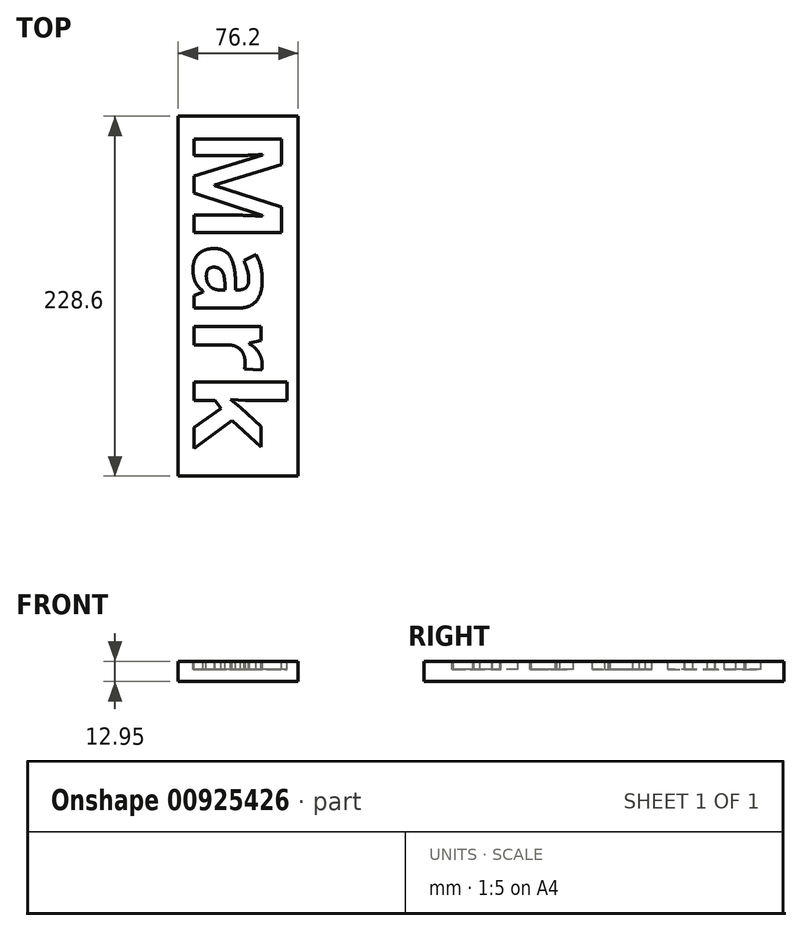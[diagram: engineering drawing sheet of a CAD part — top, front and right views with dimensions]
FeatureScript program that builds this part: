
annotation { "Feature Type Name" : "Feature", "Feature Type Description" : "" }
export const myFeature = defineFeature(function(context is Context, id is Id, definition is map)
    precondition{}
    {
        {
            var Q0;
            Q0=qCreatedBy(makeId("Front.planeOp"),FACE);
            var sketch = newSketch(context, id + "F0", { "sketchPlane" : qUnion([Q0])});
            skLineSegment(sketch, "E0.bottom", {"start": v(0, 0) * mm, "end": v(-76.2, 0) * mm});
            skLineSegment(sketch, "E0.top", {"start": v(0, 12.95) * mm, "end": v(-76.2, 12.95) * mm});
            skLineSegment(sketch, "E0.left", {"start": v(0, 0) * mm, "end": v(0, 12.95) * mm});
            skLineSegment(sketch, "E0.right", {"start": v(-76.2, 0) * mm, "end": v(-76.2, 12.95) * mm});
            skSolve(sketch);
        }
        {
            var Q0;
            Q0=makeQuery(id+"F0.imprint","IMPRINT",FACE,{"disambiguationData":[TD([[makeQuery(id+"F0.imprint","IMPRINT",EDGE,{"derivedFrom":sQuery(id+"F0.wireOp",EDGE,"E0.bottom")}),-1.0]])]});
            extrude(context, id + "F1", {"entities" : qUnion([Q0]), "depth" : 228.6 * mm, "offsetDistance" : 25.4 * mm});
        }
        {
            var Q0;
            Q0=makeQuery(id+"F1.opExtrude","SWEPT_FACE",FACE,{"disambiguationData":[OSD([sQuery(id+"F0.wireOp",EDGE,"E0.top")])]});
            var sketch = newSketch(context, id + "F2", { "sketchPlane" : qUnion([Q0])});
            skText(sketch, "E1", { "text": "Mark", "fontName": "NotoSans-Bold.ttf"});
            const initialGuessF2  = {"E1": [-0.06604, -0.00755, 0, -1, 0.05588]};
            skSetInitialGuess(sketch, initialGuessF2);
            skSolve(sketch);
        }
        {
            var Q0;
            Q0 = qSketchRegion(id + "F2", true);
            extrude(context, id + "F3", {"entities" : qUnion([Q0]), "operationType" : NewBodyOperationType.REMOVE, "oppositeDirection" : true, "depth" : 5.08 * mm, "offsetDistance" : 25.4 * mm});
        }
    });
